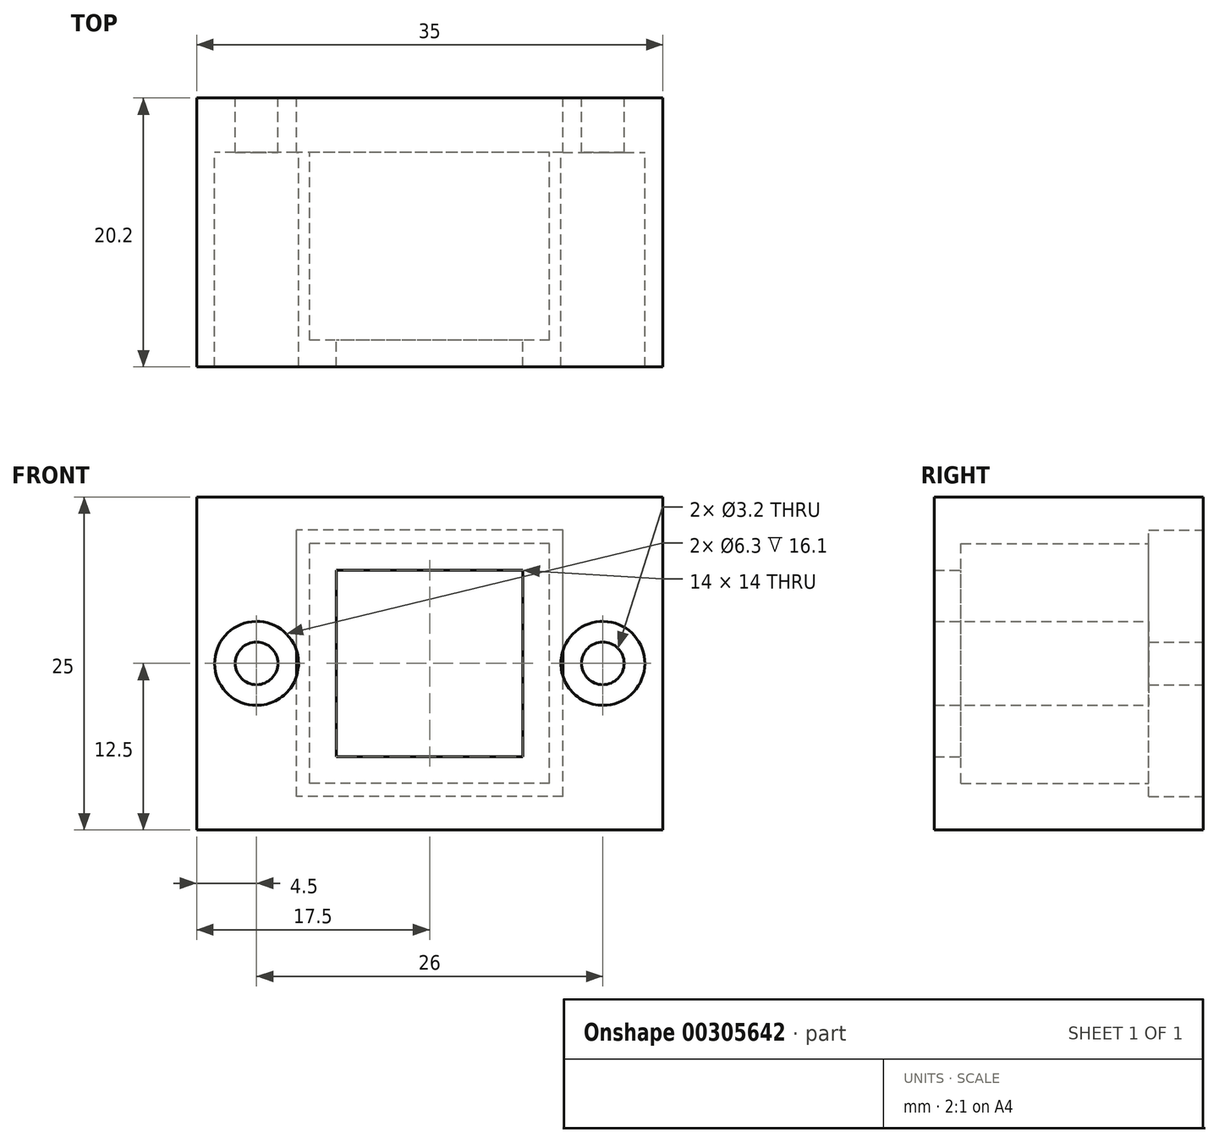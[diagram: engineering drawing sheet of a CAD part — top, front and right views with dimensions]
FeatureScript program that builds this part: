
annotation { "Feature Type Name" : "Feature", "Feature Type Description" : "" }
export const myFeature = defineFeature(function(context is Context, id is Id, definition is map)
    precondition{}
    {
        {
            var Q0;
            Q0=qCreatedBy(makeId("Front.planeOp"),FACE);
            var sketch = newSketch(context, id + "F0", { "sketchPlane" : qUnion([Q0])});
            skLineSegment(sketch, "E0.bottom", {"start": v(10, -10) * mm, "end": v(-10, -10) * mm});
            skLineSegment(sketch, "E0.top", {"start": v(10, 10) * mm, "end": v(-10, 10) * mm});
            skLineSegment(sketch, "E0.left", {"start": v(10, -10) * mm, "end": v(10, 10) * mm});
            skLineSegment(sketch, "E0.right", {"start": v(-10, -10) * mm, "end": v(-10, 10) * mm});
            skPoint(sketch, "E0.middle", {"position": v(0, 0) * mm});
            skCircle(sketch, "E1", {"center": v(-13, 0) * mm, "radius": 1.6 * mm});
            skCircle(sketch, "E2", {"center": v(13, 0) * mm, "radius": 1.6 * mm});
            skLineSegment(sketch, "E3.bottom", {"start": v(17.5, -12.5) * mm, "end": v(-17.5, -12.5) * mm});
            skLineSegment(sketch, "E3.top", {"start": v(17.5, 12.5) * mm, "end": v(-17.5, 12.5) * mm});
            skLineSegment(sketch, "E3.left", {"start": v(17.5, -12.5) * mm, "end": v(17.5, 12.5) * mm});
            skLineSegment(sketch, "E3.right", {"start": v(-17.5, -12.5) * mm, "end": v(-17.5, 12.5) * mm});
            skSolve(sketch);
        }
        {
            var Q0;
            Q0=makeQuery(id+"F0.imprint","IMPRINT",FACE,{"disambiguationData":[TD([[makeQuery(id+"F0.imprint","IMPRINT",EDGE,{"derivedFrom":sQuery(id+"F0.wireOp",EDGE,"E0.bottom")}),1.0]])]});
            extrude(context, id + "F1", {"entities" : qUnion([Q0]), "depth" : 4.1 * mm});
        }
        {
            var Q0;
            Q0=makeQuery(id+"F1.opExtrude","CAP_FACE",FACE,{"disambiguationData":[OSD([sQuery(id+"F0.wireOp",EDGE,"E0.bottom"),sQuery(id+"F0.wireOp",EDGE,"E0.top"),sQuery(id+"F0.wireOp",EDGE,"E0.left"),sQuery(id+"F0.wireOp",EDGE,"E0.right"),sQuery(id+"F0.wireOp",EDGE,"E1"),sQuery(id+"F0.wireOp",EDGE,"E2"),sQuery(id+"F0.wireOp",EDGE,"E3.bottom"),sQuery(id+"F0.wireOp",EDGE,"E3.top"),sQuery(id+"F0.wireOp",EDGE,"E3.left"),sQuery(id+"F0.wireOp",EDGE,"E3.right")])],"isStart":false});
            var sketch = newSketch(context, id + "F2", { "sketchPlane" : qUnion([Q0])});
            skLineSegment(sketch, "E4.bottom", {"start": v(9, -9) * mm, "end": v(-9, -9) * mm});
            skLineSegment(sketch, "E4.top", {"start": v(9, 9) * mm, "end": v(-9, 9) * mm});
            skLineSegment(sketch, "E4.left", {"start": v(9, -9) * mm, "end": v(9, 9) * mm});
            skLineSegment(sketch, "E4.right", {"start": v(-9, -9) * mm, "end": v(-9, 9) * mm});
            skPoint(sketch, "E4.middle", {"position": v(0, 0) * mm});
            skLineSegment(sketch, "E5.bottom", {"start": v(17.5, -12.5) * mm, "end": v(-17.5, -12.5) * mm});
            skLineSegment(sketch, "E5.top", {"start": v(17.5, 12.5) * mm, "end": v(-17.5, 12.5) * mm});
            skLineSegment(sketch, "E5.left", {"start": v(17.5, -12.5) * mm, "end": v(17.5, 12.5) * mm});
            skLineSegment(sketch, "E5.right", {"start": v(-17.5, -12.5) * mm, "end": v(-17.5, 12.5) * mm});
            skCircle(sketch, "E6", {"center": v(-13, 0) * mm, "radius": 3.15 * mm});
            skCircle(sketch, "E7", {"center": v(13, 0) * mm, "radius": 3.15 * mm});
            skSolve(sketch);
        }
        {
            var Q0;
            Q0 = qSketchRegion(id + "F2", true);
            extrude(context, id + "F3", {"entities" : qUnion([Q0]), "operationType" : NewBodyOperationType.ADD, "depth" : 14.1 * mm});
        }
        {
            var Q0;
            Q0=makeQuery(id+"F3.opExtrude","CAP_FACE",FACE,{"disambiguationData":[OSD([sQuery(id+"F2.wireOp",EDGE,"E4.bottom"),sQuery(id+"F2.wireOp",EDGE,"E4.top"),sQuery(id+"F2.wireOp",EDGE,"E4.left"),sQuery(id+"F2.wireOp",EDGE,"E4.right"),sQuery(id+"F2.wireOp",EDGE,"E5.bottom"),sQuery(id+"F2.wireOp",EDGE,"E5.top"),sQuery(id+"F2.wireOp",EDGE,"E5.left"),sQuery(id+"F2.wireOp",EDGE,"E5.right"),sQuery(id+"F2.wireOp",EDGE,"E6"),sQuery(id+"F2.wireOp",EDGE,"E7")])],"isStart":false});
            var sketch = newSketch(context, id + "F4", { "sketchPlane" : qUnion([Q0])});
            skLineSegment(sketch, "E8.bottom", {"start": v(7, -7) * mm, "end": v(-7, -7) * mm});
            skLineSegment(sketch, "E8.top", {"start": v(7, 7) * mm, "end": v(-7, 7) * mm});
            skLineSegment(sketch, "E8.left", {"start": v(7, -7) * mm, "end": v(7, 7) * mm});
            skLineSegment(sketch, "E8.right", {"start": v(-7, -7) * mm, "end": v(-7, 7) * mm});
            skPoint(sketch, "E8.middle", {"position": v(0, 0) * mm});
            skLineSegment(sketch, "E9.bottom", {"start": v(17.5, -12.5) * mm, "end": v(-17.5, -12.5) * mm});
            skLineSegment(sketch, "E9.top", {"start": v(17.5, 12.5) * mm, "end": v(-17.5, 12.5) * mm});
            skLineSegment(sketch, "E9.left", {"start": v(17.5, -12.5) * mm, "end": v(17.5, 12.5) * mm});
            skLineSegment(sketch, "E9.right", {"start": v(-17.5, -12.5) * mm, "end": v(-17.5, 12.5) * mm});
            skCircle(sketch, "E10", {"center": v(-13, 0) * mm, "radius": 3.15 * mm});
            skCircle(sketch, "E11", {"center": v(13, 0) * mm, "radius": 3.15 * mm});
            skSolve(sketch);
        }
        {
            var Q0;
            Q0 = qSketchRegion(id + "F4", true);
            extrude(context, id + "F5", {"entities" : qUnion([Q0]), "operationType" : NewBodyOperationType.ADD, "depth" : 2 * mm});
        }
        {
            var Q0;
            Q0=makeQuery(id+"F3.opExtrude","CAP_FACE",FACE,{"disambiguationData":[OSD([sQuery(id+"F2.wireOp",EDGE,"E4.bottom"),sQuery(id+"F2.wireOp",EDGE,"E4.top"),sQuery(id+"F2.wireOp",EDGE,"E4.left"),sQuery(id+"F2.wireOp",EDGE,"E4.right"),sQuery(id+"F2.wireOp",EDGE,"E5.bottom"),sQuery(id+"F2.wireOp",EDGE,"E5.top"),sQuery(id+"F2.wireOp",EDGE,"E5.left"),sQuery(id+"F2.wireOp",EDGE,"E5.right"),sQuery(id+"F2.wireOp",EDGE,"E6"),sQuery(id+"F2.wireOp",EDGE,"E7")])],"isStart":true});
            var sketch = newSketch(context, id + "F6", { "sketchPlane" : qUnion([Q0])});
            skLineSegment(sketch, "E12.bottom", {"start": v(9, -9) * mm, "end": v(-9, -9) * mm});
            skLineSegment(sketch, "E12.top", {"start": v(9, 9) * mm, "end": v(-9, 9) * mm});
            skLineSegment(sketch, "E12.left", {"start": v(9, -9) * mm, "end": v(9, 9) * mm});
            skLineSegment(sketch, "E12.right", {"start": v(-9, -9) * mm, "end": v(-9, 9) * mm});
            skPoint(sketch, "E12.middle", {"position": v(0, 0) * mm});
            skSolve(sketch);
        }
        {
            var Q0;
            Q0 = qSketchRegion(id + "F6", true);
            extrude(context, id + "F7", {"entities" : qUnion([Q0]), "operationType" : NewBodyOperationType.REMOVE, "oppositeDirection" : true, "depth" : 5 * mm});
        }
    });
